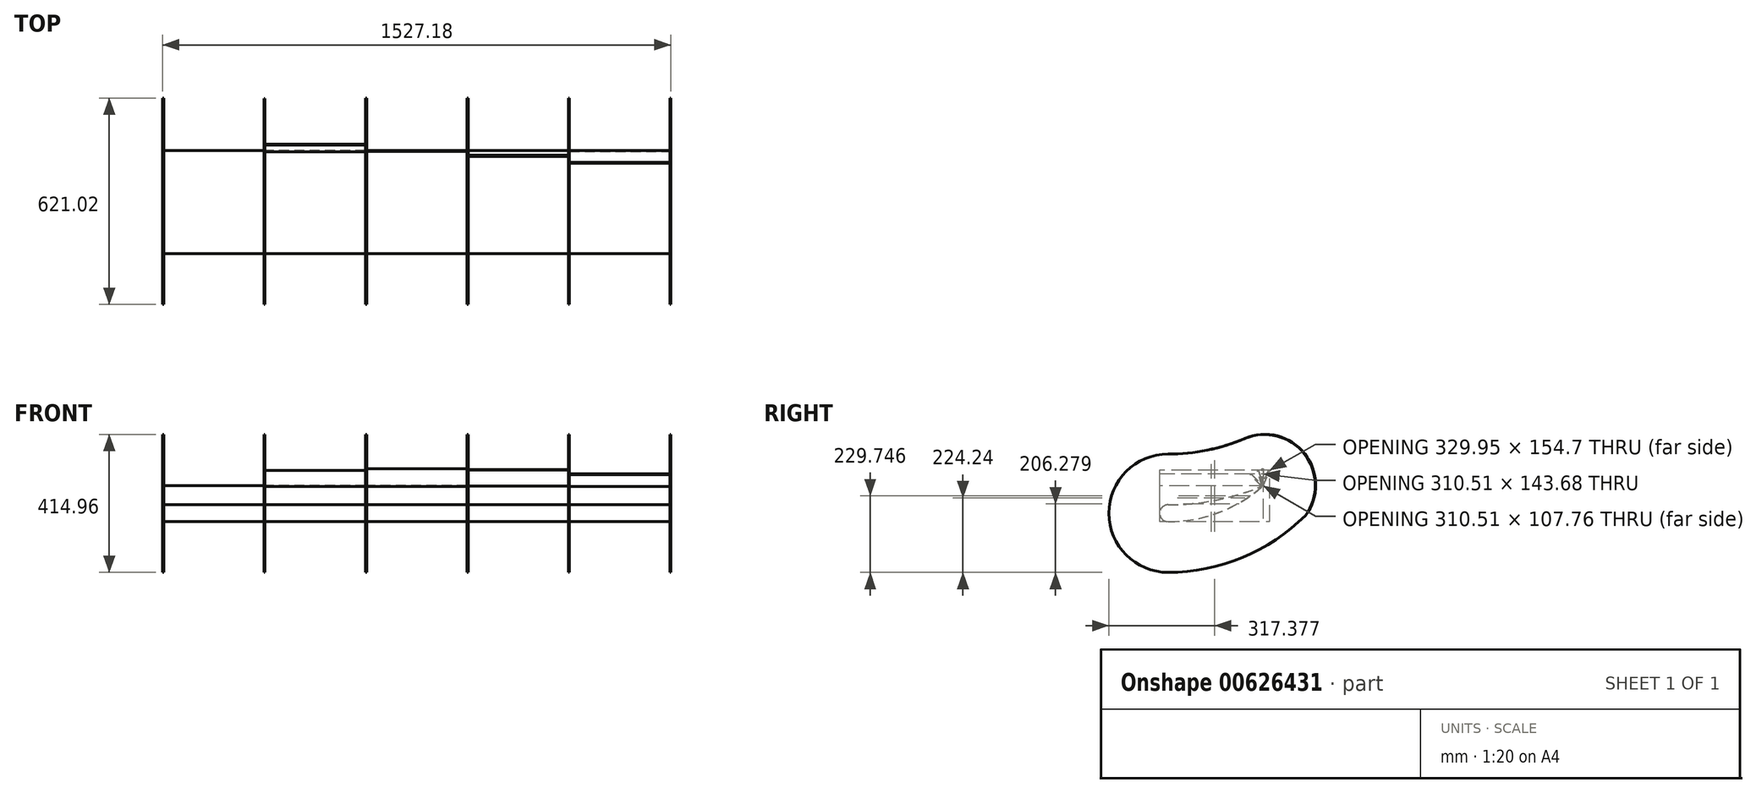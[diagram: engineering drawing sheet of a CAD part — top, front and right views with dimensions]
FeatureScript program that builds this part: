
annotation { "Feature Type Name" : "Feature", "Feature Type Description" : "" }
export const myFeature = defineFeature(function(context is Context, id is Id, definition is map)
    precondition{}
    {
        {
            var Q0;
            Q0=qCreatedBy(makeId("Right.planeOp"),FACE);
            var sketch = newSketch(context, id + "F0", { "sketchPlane" : qUnion([Q0])});
            skArc(sketch, "E0", {"start": v(0, -431.05) * mm, "mid": v(152.4, -403.21) * mm, "end": v(285.11, -323.29) * mm});
            skArc(sketch, "E1", {"start": v(0, -431.05) * mm, "mid": v(-25.4, -405.65) * mm, "end": v(0, -380.25) * mm});
            skArc(sketch, "E2", {"start": v(0, -380.25) * mm, "mid": v(145.37, -365.87) * mm, "end": v(285.11, -323.29) * mm});
            skSolve(sketch);
        }
        {
            var Q0;
            Q0 = qSketchRegion(id + "F0", true);
            extrude(context, id + "F1", {"entities" : qUnion([Q0]), "depth" : 1524 * mm, "offsetDistance" : 25.4 * mm});
        }
        {
            var Q0;
            Q0=makeQuery(id+"F1.opExtrude","CAP_VERTEX",VERTEX,{"disambiguationData":[OSD([sQuery(id+"F0.wireOp",EDGE,"E0"),sQuery(id+"F0.wireOp",EDGE,"E1"),sQuery(id+"F0.wireOp",EDGE,"b3eccc3d-6429-4b34-9fe6-7e9520ef1e49")])],"isStart":false});
            var Q1;
            Q1=makeQuery(id+"F1.opExtrude","CAP_VERTEX",VERTEX,{"disambiguationData":[OSD([sQuery(id+"F0.wireOp",EDGE,"E1"),sQuery(id+"F0.wireOp",EDGE,"E2"),sQuery(id+"F0.wireOp",EDGE,"b3eccc3d-6429-4b34-9fe6-7e9520ef1e49")])],"isStart":false});
            var Q2;
            Q2=makeQuery(id+"F1.opExtrude","CAP_VERTEX",VERTEX,{"disambiguationData":[OSD([sQuery(id+"F0.wireOp",EDGE,"E0"),sQuery(id+"F0.wireOp",EDGE,"E2")])],"isStart":false});
            cPlane(context, id + "F2", {"entities" : qUnion([Q0, Q1, Q2]), "cplaneType" : CPlaneType.THREE_POINT, "offset" : 25.4 * mm, "width" : 152.4 * mm, "height" : 152.4 * mm});
        }
        {
            var Q0;
            Q0=qCreatedBy(id+"F2.planeOp",FACE);
            var sketch = newSketch(context, id + "F3", { "sketchPlane" : qUnion([Q0])});
            skLineSegment(sketch, "E3", {"start": v(285.11, -323.29) * mm, "end": v(249.2, -287.37) * mm});
            skLineSegment(sketch, "E4", {"start": v(249.2, -287.37) * mm, "end": v(246.95, -289.61) * mm});
            skLineSegment(sketch, "E5", {"start": v(246.95, -289.61) * mm, "end": v(282.95, -325.62) * mm});
            skLineSegment(sketch, "E6", {"start": v(285.11, -323.29) * mm, "end": v(282.95, -325.62) * mm});
            skSolve(sketch);
        }
        {
            var Q0;
            Q0=makeQuery(id+"F3.imprint","IMPRINT",FACE,{"disambiguationData":[TD([[makeQuery(id+"F3.imprint","IMPRINT",EDGE,{"derivedFrom":sQuery(id+"F3.wireOp",EDGE,"E3")}),1.0]])]});
            extrude(context, id + "F4", {"entities" : qUnion([Q0]), "operationType" : NewBodyOperationType.ADD, "oppositeDirection" : true, "depth" : 304.8 * mm, "offsetDistance" : 25.4 * mm});
        }
        {
            var Q0;
            Q0=qCreatedBy(id+"F2.planeOp",FACE);
            cPlane(context, id + "F5", {"entities" : qUnion([Q0]), "cplaneType" : CPlaneType.OFFSET, "offset" : 304.8 * mm, "oppositeDirection" : true, "width" : 152.4 * mm, "height" : 152.4 * mm});
        }
        {
            var Q0;
            Q0=qCreatedBy(id+"F5.planeOp",FACE);
            var sketch = newSketch(context, id + "F6", { "sketchPlane" : qUnion([Q0])});
            skPoint(sketch, "E7.0", {"position": v(285.11, -323.29) * mm});
            skLineSegment(sketch, "E8", {"start": v(285.11, -323.29) * mm, "end": v(270.88, -274.52) * mm});
            skLineSegment(sketch, "E9", {"start": v(270.88, -274.52) * mm, "end": v(267.83, -275.41) * mm});
            skLineSegment(sketch, "E10", {"start": v(267.83, -275.41) * mm, "end": v(282.42, -325.4) * mm});
            skLineSegment(sketch, "E11", {"start": v(282.42, -325.4) * mm, "end": v(285.11, -323.29) * mm});
            skSolve(sketch);
        }
        {
            var Q0;
            Q0 = qSketchRegion(id + "F6", true);
            extrude(context, id + "F7", {"entities" : qUnion([Q0]), "operationType" : NewBodyOperationType.ADD, "oppositeDirection" : true, "depth" : 304.8 * mm, "offsetDistance" : 25.4 * mm});
        }
        {
            var Q0;
            Q0=qCreatedBy(id+"F5.planeOp",FACE);
            cPlane(context, id + "F8", {"entities" : qUnion([Q0]), "cplaneType" : CPlaneType.OFFSET, "offset" : 304.8 * mm, "oppositeDirection" : true, "width" : 152.4 * mm, "height" : 152.4 * mm});
        }
        {
            var Q0;
            Q0=qCreatedBy(id+"F8.planeOp",FACE);
            var sketch = newSketch(context, id + "F9", { "sketchPlane" : qUnion([Q0])});
            skPoint(sketch, "E12.0", {"position": v(285.11, -323.29) * mm});
            skLineSegment(sketch, "E13", {"start": v(285.11, -323.29) * mm, "end": v(285.11, -272.49) * mm});
            skLineSegment(sketch, "E14", {"start": v(285.11, -272.49) * mm, "end": v(281.94, -272.49) * mm});
            skLineSegment(sketch, "E15", {"start": v(281.94, -272.49) * mm, "end": v(281.94, -325.83) * mm});
            skLineSegment(sketch, "E16", {"start": v(281.94, -325.83) * mm, "end": v(285.11, -323.29) * mm});
            skSolve(sketch);
        }
        {
            var Q0;
            Q0 = qSketchRegion(id + "F9", true);
            extrude(context, id + "F10", {"entities" : qUnion([Q0]), "operationType" : NewBodyOperationType.ADD, "oppositeDirection" : true, "depth" : 304.8 * mm, "offsetDistance" : 25.4 * mm});
        }
        {
            var Q0;
            Q0=qCreatedBy(id+"F8.planeOp",FACE);
            cPlane(context, id + "F11", {"entities" : qUnion([Q0]), "cplaneType" : CPlaneType.OFFSET, "offset" : 304.8 * mm, "oppositeDirection" : true, "width" : 152.4 * mm, "height" : 152.4 * mm});
        }
        {
            var Q0;
            Q0=qCreatedBy(id+"F11.planeOp",FACE);
            cPlane(context, id + "F12", {"entities" : qUnion([Q0]), "cplaneType" : CPlaneType.OFFSET, "offset" : 304.8 * mm, "oppositeDirection" : true, "width" : 152.4 * mm, "height" : 152.4 * mm});
        }
        {
            var Q0;
            Q0=makeQuery(id+"F1.opExtrude","CAP_FACE",FACE,{"disambiguationData":[OSD([sQuery(id+"F0.wireOp",EDGE,"E0"),sQuery(id+"F0.wireOp",EDGE,"E1"),sQuery(id+"F0.wireOp",EDGE,"E2")])],"isStart":true});
            var sketch = newSketch(context, id + "F13", { "sketchPlane" : qUnion([Q0])});
            skArc(sketch, "E17.0", {"start": v(0, -227.85) * mm, "mid": v(-117.93, -215.94) * mm, "end": v(-231.1, -180.68) * mm});
            skArc(sketch, "E18.0", {"start": v(0, -583.45) * mm, "mid": v(177.8, -405.65) * mm, "end": v(0, -227.85) * mm});
            skArc(sketch, "E19.0", {"start": v(0, -583.45) * mm, "mid": v(-223.28, -539.04) * mm, "end": v(-412.56, -412.56) * mm});
            skArc(sketch, "E20", {"start": v(-231.1, -180.68) * mm, "mid": v(-410.84, -226.96) * mm, "end": v(-412.56, -412.56) * mm});
            skSolve(sketch);
        }
        {
            var Q0;
            Q0 = qSketchRegion(id + "F13", true);
            extrude(context, id + "F14", {"entities" : qUnion([Q0]), "operationType" : NewBodyOperationType.ADD, "endBound" : BoundingType.SYMMETRIC, "depth" : 3.17 * mm, "offsetDistance" : 25.4 * mm});
        }
        {
            var Q0;
            Q0=qCreatedBy(id+"F11.planeOp",FACE);
            var sketch = newSketch(context, id + "F15", { "sketchPlane" : qUnion([Q0])});
            skArc(sketch, "E21.0", {"start": v(0, -227.85) * mm, "mid": v(117.17, -216.1) * mm, "end": v(229.67, -181.28) * mm});
            skArc(sketch, "E22.0", {"start": v(0, -583.45) * mm, "mid": v(223.28, -539.04) * mm, "end": v(412.56, -412.56) * mm});
            skArc(sketch, "E23", {"start": v(0, -227.85) * mm, "mid": v(-177.8, -405.65) * mm, "end": v(0, -583.45) * mm});
            skArc(sketch, "E24", {"start": v(229.67, -181.28) * mm, "mid": v(409.2, -227.27) * mm, "end": v(412.56, -412.56) * mm});
            skSolve(sketch);
        }
        {
            var Q0;
            Q0 = qSketchRegion(id + "F15", true);
            extrude(context, id + "F16", {"entities" : qUnion([Q0]), "operationType" : NewBodyOperationType.ADD, "endBound" : BoundingType.SYMMETRIC, "depth" : 3.17 * mm, "offsetDistance" : 25.4 * mm});
        }
        {
            var Q0;
            Q0=qCreatedBy(id+"F8.planeOp",FACE);
            var sketch = newSketch(context, id + "F17", { "sketchPlane" : qUnion([Q0])});
            skArc(sketch, "E25.0", {"start": v(0, -227.85) * mm, "mid": v(117.17, -216.1) * mm, "end": v(229.67, -181.28) * mm});
            skArc(sketch, "E26.0", {"start": v(0, -583.45) * mm, "mid": v(223.28, -539.04) * mm, "end": v(412.56, -412.56) * mm});
            skArc(sketch, "E27", {"start": v(0, -227.85) * mm, "mid": v(-177.8, -405.65) * mm, "end": v(0, -583.45) * mm});
            skArc(sketch, "E28", {"start": v(229.67, -181.28) * mm, "mid": v(409.2, -227.27) * mm, "end": v(412.56, -412.56) * mm});
            skSolve(sketch);
        }
        {
            var Q0;
            Q0 = qSketchRegion(id + "F17", true);
            extrude(context, id + "F18", {"entities" : qUnion([Q0]), "operationType" : NewBodyOperationType.ADD, "endBound" : BoundingType.SYMMETRIC, "depth" : 3.17 * mm, "offsetDistance" : 25.4 * mm});
        }
        {
            var Q0;
            Q0=qCreatedBy(id+"F5.planeOp",FACE);
            var sketch = newSketch(context, id + "F19", { "sketchPlane" : qUnion([Q0])});
            skArc(sketch, "E29.0", {"start": v(0, -227.85) * mm, "mid": v(117.17, -216.1) * mm, "end": v(229.67, -181.28) * mm});
            skArc(sketch, "E30.0", {"start": v(0, -583.45) * mm, "mid": v(223.28, -539.04) * mm, "end": v(412.56, -412.56) * mm});
            skArc(sketch, "E31", {"start": v(0, -227.85) * mm, "mid": v(-177.8, -405.65) * mm, "end": v(0, -583.45) * mm});
            skArc(sketch, "E32", {"start": v(229.67, -181.28) * mm, "mid": v(409.2, -227.27) * mm, "end": v(412.56, -412.56) * mm});
            skSolve(sketch);
        }
        {
            var Q0;
            Q0 = qSketchRegion(id + "F19", true);
            extrude(context, id + "F20", {"entities" : qUnion([Q0]), "operationType" : NewBodyOperationType.ADD, "endBound" : BoundingType.SYMMETRIC, "depth" : 3.17 * mm, "offsetDistance" : 25.4 * mm});
        }
        {
            var Q0;
            Q0=qCreatedBy(id+"F2.planeOp",FACE);
            var sketch = newSketch(context, id + "F21", { "sketchPlane" : qUnion([Q0])});
            skArc(sketch, "E33.0", {"start": v(0, -227.85) * mm, "mid": v(117.17, -216.1) * mm, "end": v(229.67, -181.28) * mm});
            skArc(sketch, "E34.0", {"start": v(0, -583.45) * mm, "mid": v(223.28, -539.04) * mm, "end": v(412.56, -412.56) * mm});
            skArc(sketch, "E35", {"start": v(0, -227.85) * mm, "mid": v(-177.8, -405.65) * mm, "end": v(0, -583.45) * mm});
            skArc(sketch, "E36", {"start": v(229.67, -181.28) * mm, "mid": v(409.2, -227.27) * mm, "end": v(412.56, -412.56) * mm});
            skSolve(sketch);
        }
        {
            var Q0;
            Q0 = qSketchRegion(id + "F21", true);
            extrude(context, id + "F22", {"entities" : qUnion([Q0]), "operationType" : NewBodyOperationType.ADD, "endBound" : BoundingType.SYMMETRIC, "depth" : 3.17 * mm, "offsetDistance" : 25.4 * mm});
        }
        {
            var Q0;
            Q0=qCreatedBy(id+"F11.planeOp",FACE);
            var sketch = newSketch(context, id + "F23", { "sketchPlane" : qUnion([Q0])});
            skPoint(sketch, "E37.0", {"position": v(285.11, -323.29) * mm});
            skLineSegment(sketch, "E38", {"start": v(285.11, -323.29) * mm, "end": v(304.55, -276.36) * mm});
            skLineSegment(sketch, "E39", {"start": v(304.55, -276.36) * mm, "end": v(301.38, -276.36) * mm});
            skLineSegment(sketch, "E40", {"start": v(301.38, -276.36) * mm, "end": v(280.97, -325.64) * mm});
            skLineSegment(sketch, "E41", {"start": v(280.97, -325.64) * mm, "end": v(285.11, -323.29) * mm});
            skSolve(sketch);
        }
        {
            var Q0;
            Q0 = qSketchRegion(id + "F23", true);
            extrude(context, id + "F24", {"entities" : qUnion([Q0]), "operationType" : NewBodyOperationType.ADD, "oppositeDirection" : true, "depth" : 304.8 * mm, "offsetDistance" : 25.4 * mm});
        }
        {
            var Q0;
            Q0=qCreatedBy(id+"F12.planeOp",FACE);
            var sketch = newSketch(context, id + "F25", { "sketchPlane" : qUnion([Q0])});
            skArc(sketch, "E42.0", {"start": v(0, -227.85) * mm, "mid": v(116.88, -216.15) * mm, "end": v(229.12, -181.51) * mm});
            skArc(sketch, "E43.0", {"start": v(0, -583.45) * mm, "mid": v(223.28, -539.04) * mm, "end": v(412.56, -412.56) * mm});
            skArc(sketch, "E44", {"start": v(0, -227.85) * mm, "mid": v(-177.8, -405.65) * mm, "end": v(0, -583.45) * mm});
            skArc(sketch, "E45", {"start": v(229.12, -181.51) * mm, "mid": v(408.56, -227.4) * mm, "end": v(412.56, -412.56) * mm});
            skSolve(sketch);
        }
        {
            var Q0;
            Q0 = qSketchRegion(id + "F25", true);
            extrude(context, id + "F26", {"entities" : qUnion([Q0]), "operationType" : NewBodyOperationType.ADD, "endBound" : BoundingType.SYMMETRIC, "depth" : 3.17 * mm, "offsetDistance" : 25.4 * mm});
        }
    });
